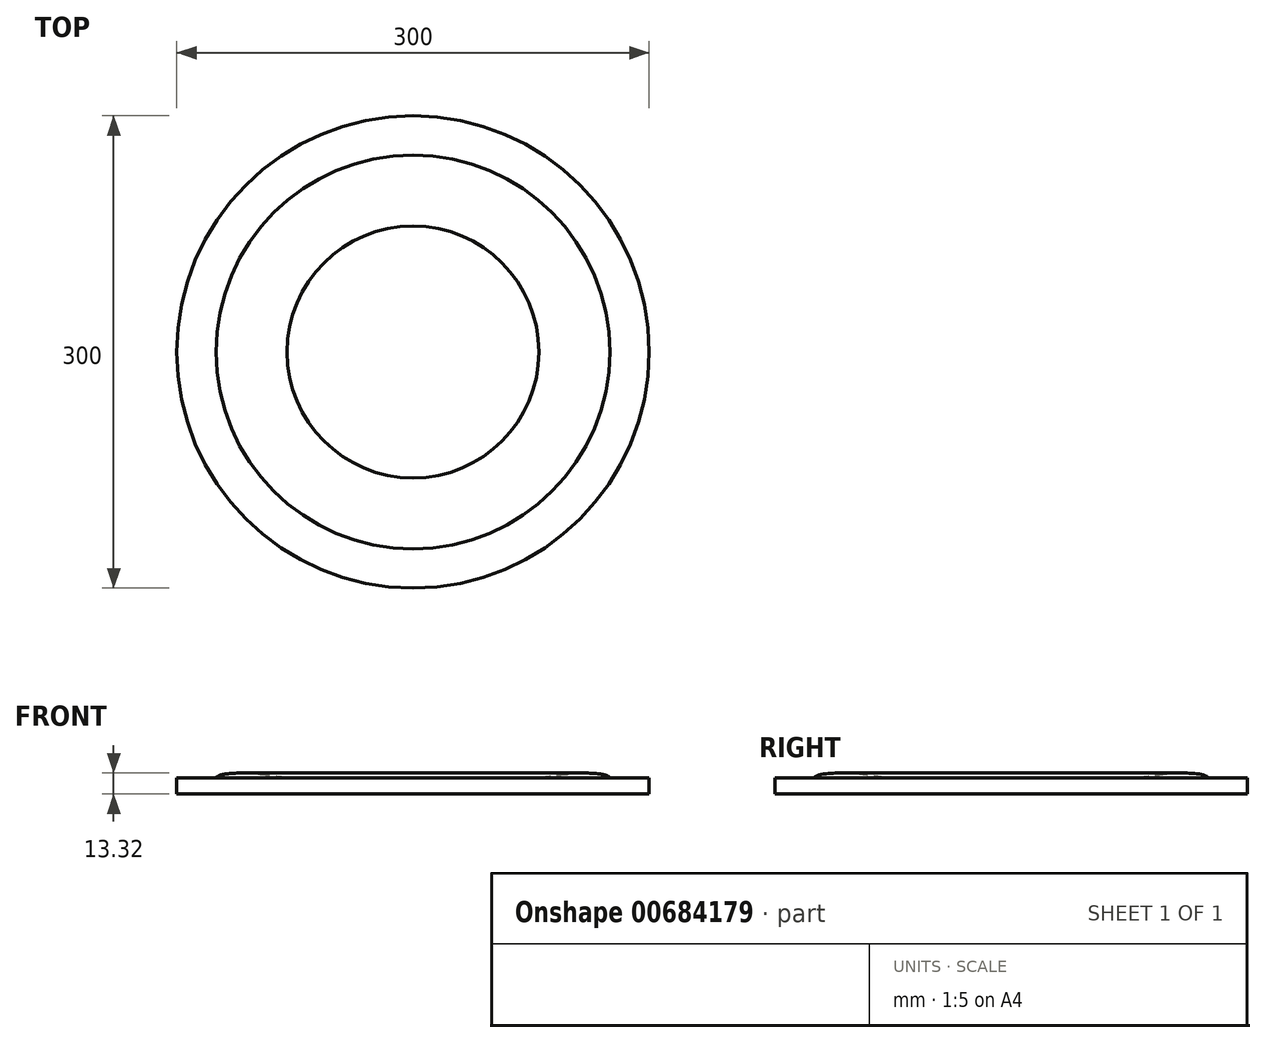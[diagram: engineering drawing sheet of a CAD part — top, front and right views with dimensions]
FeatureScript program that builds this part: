
annotation { "Feature Type Name" : "Feature", "Feature Type Description" : "" }
export const myFeature = defineFeature(function(context is Context, id is Id, definition is map)
    precondition{}
    {
        {
            var Q0;
            Q0=qCreatedBy(makeId("Front.planeOp"),FACE);
            var sketch = newSketch(context, id + "F0", { "sketchPlane" : qUnion([Q0])});
            skLineSegment(sketch, "E0", {"start": v(0, 0) * mm, "end": v(-80, 0) * mm});
            skFitSpline(sketch, "E1", {"points": [v(-125.06, 0) * mm, v(-124, 1.17) * mm, v(-112.4, 3.09) * mm, v(-96.7, 2.3) * mm, v(-86.39, 1.2) * mm, v(-82.66, 0.75) * mm, v(-80.4, 0.24) * mm, v(-80, 0) * mm], "startDerivative": vector(2.13, 10.31) * mm, "endDerivative": vector(9.53, -6.08) * mm});
            skLineSegment(sketch, "E2.trimOffspring", {"start": v(-125.06, 0) * mm, "end": v(-150, 0) * mm});
            skLineSegment(sketch, "E3", {"start": v(-150, 0) * mm, "end": v(-150, -10.2) * mm});
            skLineSegment(sketch, "E4", {"start": v(-150, -10.2) * mm, "end": v(0, -10.2) * mm});
            skLineSegment(sketch, "E5", {"start": v(0, -10.2) * mm, "end": v(0, 0) * mm});
            skSolve(sketch);
        }
        {
            var Q0;
            Q0 = qSketchRegion(id + "F0", true);
            var Q1;
            Q1=sQuery(id+"F0.wireOp",EDGE,"E5");
            revolve(context, id + "F1", {"entities" : qUnion([Q0]), "axis" : qUnion([Q1]), "revolveType" : RevolveType.FULL});
        }
    });
